# Revit family: D200
name_source: partatom
category: Duct Accessories
revit_build: Autodesk Revit 2018 (Build: 20170223_1515(x64)
units: mm (PartAtom-declared; Revit-internal decimal feet)

## family parameters
Always vertical = Yes
Cut with Voids When Loaded = No
OmniClass Number = 23.75.70.11.14.14
OmniClass Title = Dampers for Air Ductwork
Part Type = Damper
Round Connector Dimension = Use Diameter
Shared = No
Work Plane-Based = No

## types (1)
- GRYFIT CX-5, D=200, Galvanized steel, FDG-WT-8-24, D=200. P=390
    Access door = No
    Actuator type. = FDG-WT-8
    Actuator voltage. = 24/48 V AC/DC
    Application in mixed systems (SM) = No
    Assembly in light wall = No
    Compact index = No
    Damper Length = 150 mm
    Damper Material = <By Category>
    Damper casing tightness class. = C (EN 1751:2002)
    Damper tightness class. = 4 (EN 1751:2002)
    Diameter (D). = 200
    Double Beginning and End (2WKKP) = None
    EMS module = No
    EPDM Gaskets = No
    Electromagnet = No
    Fire resistance class. = EI 120(ve-ho-i<->o)S (EN 13501-3+A1:2010)
    Geometry = GRYFIT CX-5, D=200, Galvanized steel, FDG-WT-8-24, D=200. P=390
    Half Damper Length = 75 mm  [stored 0.246063 ft]
    Installation Brackets = No
    Installation opening diam. (Dr). = 250
    Length (P). = 390
    Material. = Galvanized steel
    Mechanism cover = No
    Thickness of wall (G). = 115
    Type. = GRYFIT CX-5
    Without function separation (BRF) = Yes
    anglXY1 = 180.00°
    anglXY2 = 0.00°
    anglZ1 = 0.00°
    anglZ2 = 0.00°
    diamcon1 = 200 mm
    diamcon2 = 200 mm
    lengX1 = 0 mm  [stored 0 ft]
    lengX2 = 195 mm  [stored 0.639764 ft]
    lengXY1 = 600 mm  [stored 1.9685 ft]
    lengXY2 = 800 mm  [stored 2.62467 ft]
    lengXYZ1 = 500 mm  [stored 1.64042 ft]
    lengXYZ2 = 605 mm
    lengY1 = 0 mm  [stored 0 ft]
    lengY2 = 0 mm  [stored 0 ft]
    lengZ1 = 0 mm  [stored 0 ft]
    lengZ2 = 0 mm  [stored 0 ft]

note: [stored X ft] marks values corroborated as IEEE doubles in the binary element streams (Revit-internal decimal feet)

## geometry (parser evidence)
native form markers: Sweep x6
no freeform markers — native parametric forms only
